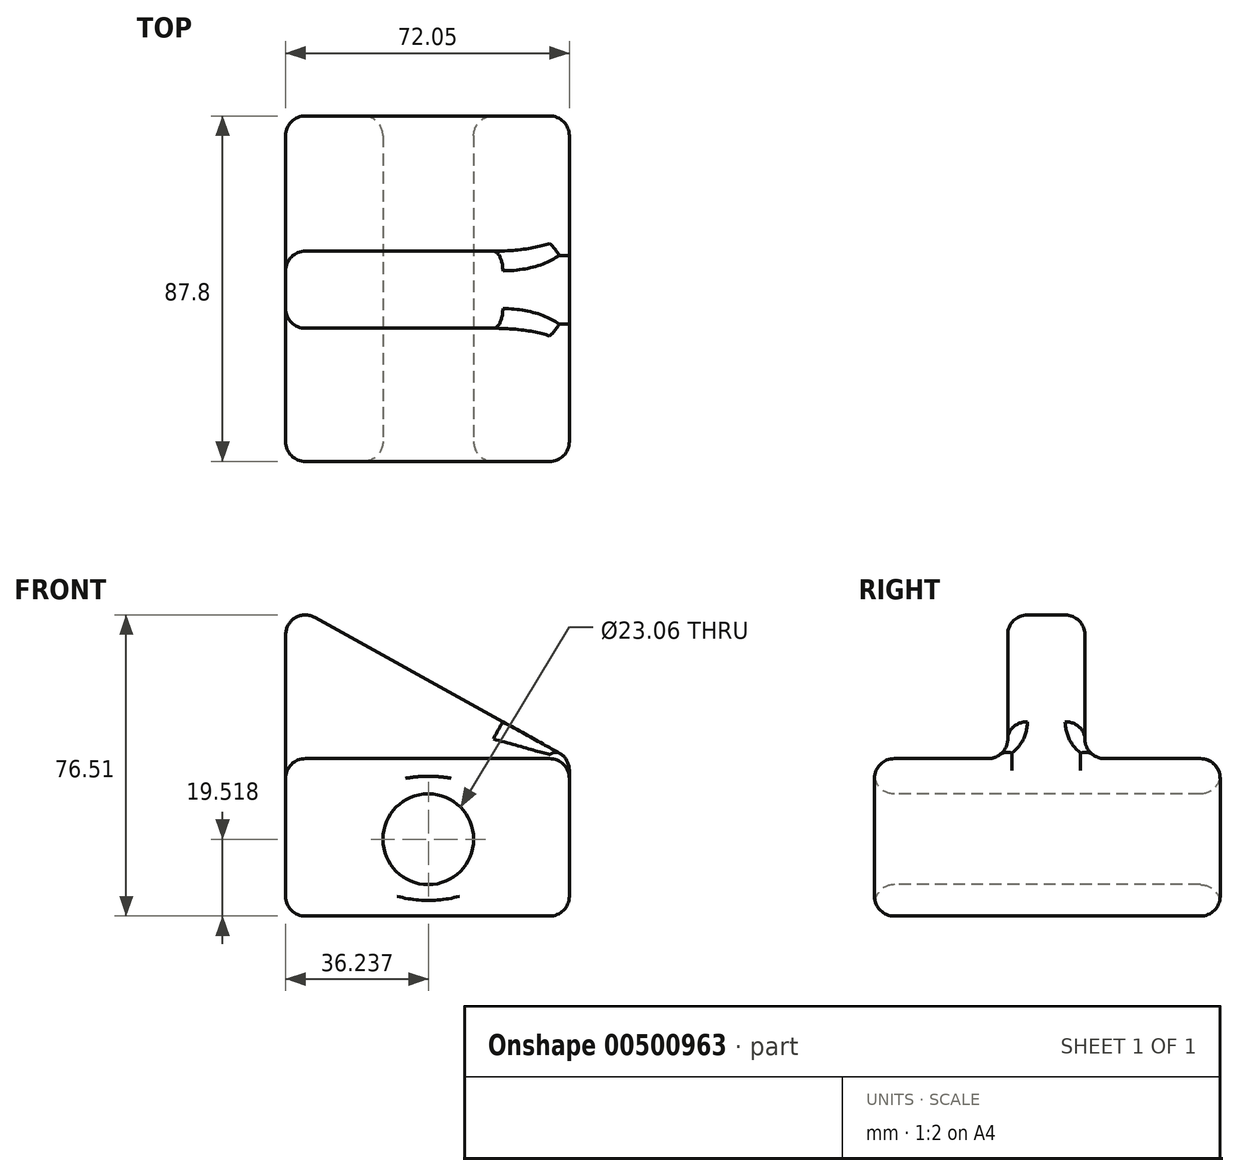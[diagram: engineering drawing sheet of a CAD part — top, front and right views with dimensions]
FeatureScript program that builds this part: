
annotation { "Feature Type Name" : "Feature", "Feature Type Description" : "" }
export const myFeature = defineFeature(function(context is Context, id is Id, definition is map)
    precondition{}
    {
        {
            var Q0;
            Q0=qCreatedBy(makeId("Top.planeOp"),FACE);
            var sketch = newSketch(context, id + "F0", { "sketchPlane" : qUnion([Q0])});
            skLineSegment(sketch, "E0.bottom", {"start": v(-59.89, -44.54) * mm, "end": v(12.16, -44.54) * mm});
            skLineSegment(sketch, "E0.top", {"start": v(-59.89, 43.26) * mm, "end": v(12.16, 43.26) * mm});
            skLineSegment(sketch, "E0.left", {"start": v(-59.89, -44.54) * mm, "end": v(-59.89, 43.26) * mm});
            skLineSegment(sketch, "E0.right", {"start": v(12.16, -44.54) * mm, "end": v(12.16, 43.26) * mm});
            skSolve(sketch);
        }
        {
            var Q0;
            Q0=makeQuery(id+"F0.imprint","IMPRINT",FACE,{"disambiguationData":[TD([[makeQuery(id+"F0.imprint","IMPRINT",EDGE,{"derivedFrom":sQuery(id+"F0.wireOp",EDGE,"E0.bottom")}),1.0]])]});
            extrude(context, id + "F1", {"entities" : qUnion([Q0]), "depth" : 40 * mm});
        }
        {
            var Q0;
            Q0=makeQuery(id+"F1.opExtrude","SWEPT_FACE",FACE,{"disambiguationData":[OSD([sQuery(id+"F0.wireOp",EDGE,"E0.bottom")])]});
            var sketch = newSketch(context, id + "F2", { "sketchPlane" : qUnion([Q0])});
            skCircle(sketch, "E1", {"center": v(-23.65, 19.52) * mm, "radius": 11.53 * mm});
            skSolve(sketch);
        }
        {
            var Q0;
            Q0=makeQuery(id+"F2.imprint","IMPRINT",FACE,{"disambiguationData":[TD([[makeQuery(id+"F2.imprint","IMPRINT",EDGE,{"derivedFrom":sQuery(id+"F2.wireOp",EDGE,"E1")}),1.0]])]});
            extrude(context, id + "F3", {"entities" : qUnion([Q0]), "operationType" : NewBodyOperationType.REMOVE, "endBound" : BoundingType.THROUGH_ALL, "oppositeDirection" : true, "depth" : 25 * mm});
        }
        {
            var Q0;
            Q0=makeQuery(id+"F1.opExtrude","CAP_FACE",FACE,{"disambiguationData":[OSD([sQuery(id+"F0.wireOp",EDGE,"E0.bottom"),sQuery(id+"F0.wireOp",EDGE,"E0.top"),sQuery(id+"F0.wireOp",EDGE,"E0.left"),sQuery(id+"F0.wireOp",EDGE,"E0.right")])],"isStart":false});
            var sketch = newSketch(context, id + "F4", { "sketchPlane" : qUnion([Q0])});
            skLineSegment(sketch, "E2.bottom", {"start": v(-59.89, -10.7) * mm, "end": v(12.16, -10.7) * mm});
            skLineSegment(sketch, "E2.top", {"start": v(-59.89, 8.88) * mm, "end": v(12.16, 8.88) * mm});
            skLineSegment(sketch, "E2.left", {"start": v(-59.89, -10.7) * mm, "end": v(-59.89, 8.88) * mm});
            skLineSegment(sketch, "E2.right", {"start": v(12.16, -10.7) * mm, "end": v(12.16, 8.88) * mm});
            skSolve(sketch);
        }
        {
            var Q0;
            Q0=makeQuery(id+"F4.imprint","IMPRINT",FACE,{"disambiguationData":[TD([[makeQuery(id+"F4.imprint","IMPRINT",EDGE,{"derivedFrom":sQuery(id+"F4.wireOp",EDGE,"E2.bottom")}),1.0]])]});
            extrude(context, id + "F5", {"entities" : qUnion([Q0]), "operationType" : NewBodyOperationType.ADD, "depth" : 40 * mm});
        }
        {
            var Q0;
            Q0=makeQuery(id+"F5.opExtrude","SWEPT_FACE",FACE,{"disambiguationData":[OSD([sQuery(id+"F4.wireOp",EDGE,"E2.bottom")])]});
            var sketch = newSketch(context, id + "F6", { "sketchPlane" : qUnion([Q0])});
            skLineSegment(sketch, "E3", {"start": v(12.16, 40) * mm, "end": v(-59.89, 80) * mm});
            skSolve(sketch);
        }
        {
            var Q0;
            Q0=makeQuery(id+"F6.imprint","IMPRINT",FACE,{"disambiguationData":[TD([[makeQuery(id+"F6.imprint","IMPRINT",EDGE,{"derivedFrom":sQuery(id+"F6.wireOp",EDGE,"E3")}),-1.0]])]});
            extrude(context, id + "F7", {"entities" : qUnion([Q0]), "operationType" : NewBodyOperationType.REMOVE, "endBound" : BoundingType.THROUGH_ALL, "oppositeDirection" : true, "depth" : 25 * mm});
        }
        {
            var Q0;
            Q0=makeQuery(id+"F1.opExtrude","SWEPT_FACE",FACE,{"disambiguationData":[OSD([sQuery(id+"F0.wireOp",EDGE,"E0.bottom")])]});
            var Q1;
            Q1=makeQuery(id+"F5.boolean.opBoolean","MERGE",FACE,{"derivedFrom":[makeQuery(id+"F1.opExtrude","SWEPT_FACE",FACE,{"disambiguationData":[OSD([sQuery(id+"F0.wireOp",EDGE,"E0.right")])]}),makeQuery(id+"F5.opExtrude","SWEPT_FACE",FACE,{"disambiguationData":[OSD([sQuery(id+"F4.wireOp",EDGE,"E2.right")])]})]});
            var Q2;
            {var subQ0=sQuery(id+"F0.wireOp",EDGE,"E0.right");var subQ1=sQuery(id+"F0.wireOp",EDGE,"E0.left");var subQ2=sQuery(id+"F0.wireOp",EDGE,"E0.top");Q2=makeQuery(id+"F5.boolean.opBoolean","SPLIT",FACE,{"disambiguationData":[TD([makeQuery(id+"F1.opExtrude","SWEPT_FACE",FACE,{"disambiguationData":[OSD([subQ2])]})])],"derivedFrom":makeQuery(id+"F1.opExtrude","CAP_FACE",FACE,{"disambiguationData":[OSD([sQuery(id+"F0.wireOp",EDGE,"E0.bottom"),subQ2,subQ1,subQ0])],"isStart":false})});}
            var Q3;
            Q3=makeQuery(id+"F7.boolean.opBoolean","COPY",FACE,{"derivedFrom":makeQuery(id+"F7.opExtrude","SWEPT_FACE",FACE,{"disambiguationData":[OSD([sQuery(id+"F6.wireOp",EDGE,"E3")])]})});
            var Q4;
            Q4=makeQuery(id+"F5.opExtrude","SWEPT_FACE",FACE,{"disambiguationData":[OSD([sQuery(id+"F4.wireOp",EDGE,"E2.bottom")])]});
            var Q5;
            {var subQ0=sQuery(id+"F0.wireOp",EDGE,"E0.left");var subQ1=sQuery(id+"F0.wireOp",EDGE,"E0.right");var subQ2=sQuery(id+"F0.wireOp",EDGE,"E0.bottom");Q5=makeQuery(id+"F5.boolean.opBoolean","SPLIT",FACE,{"disambiguationData":[TD([makeQuery(id+"F1.opExtrude","SWEPT_FACE",FACE,{"disambiguationData":[OSD([subQ2])]})])],"derivedFrom":makeQuery(id+"F1.opExtrude","CAP_FACE",FACE,{"disambiguationData":[OSD([subQ2,sQuery(id+"F0.wireOp",EDGE,"E0.top"),subQ0,subQ1])],"isStart":false})});}
            var Q6;
            Q6=makeQuery(id+"F5.boolean.opBoolean","MERGE",FACE,{"derivedFrom":[makeQuery(id+"F1.opExtrude","SWEPT_FACE",FACE,{"disambiguationData":[OSD([sQuery(id+"F0.wireOp",EDGE,"E0.left")])]}),makeQuery(id+"F5.opExtrude","SWEPT_FACE",FACE,{"disambiguationData":[OSD([sQuery(id+"F4.wireOp",EDGE,"E2.left")])]})]});
            var Q7;
            Q7=makeQuery(id+"F1.opExtrude","CAP_FACE",FACE,{"disambiguationData":[OSD([sQuery(id+"F0.wireOp",EDGE,"E0.bottom"),sQuery(id+"F0.wireOp",EDGE,"E0.top"),sQuery(id+"F0.wireOp",EDGE,"E0.left"),sQuery(id+"F0.wireOp",EDGE,"E0.right")])],"isStart":true});
            var Q8;
            Q8=makeQuery(id+"F1.opExtrude","SWEPT_FACE",FACE,{"disambiguationData":[OSD([sQuery(id+"F0.wireOp",EDGE,"E0.top")])]});
            fillet(context, id + "F8", {"entities" : qUnion([Q0, Q1, Q2, Q3, Q4, Q5, Q6, Q7, Q8]), "radius" : 5 * mm, "tangentPropagation" : true, "allowEdgeOverflow" : false});
        }
    });
